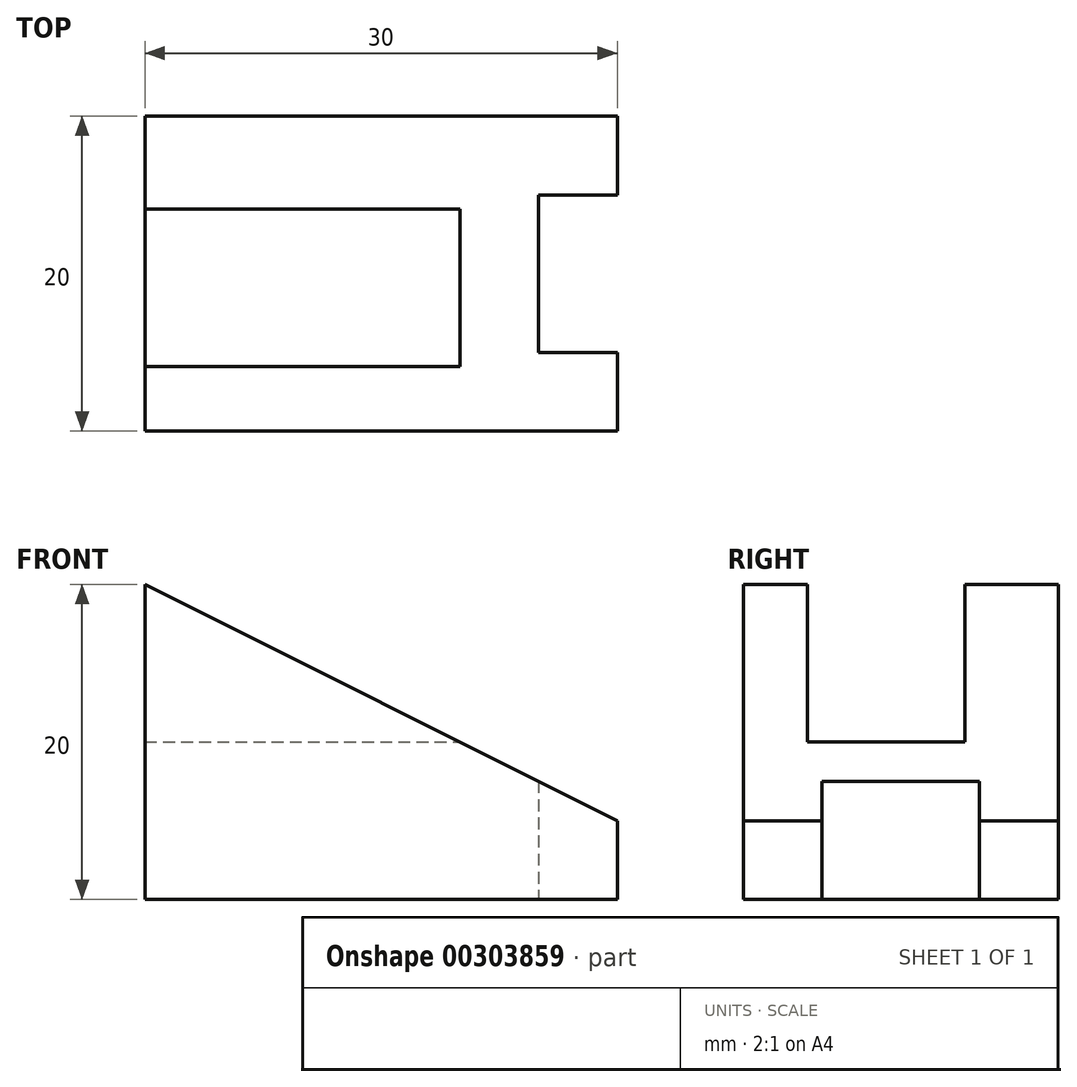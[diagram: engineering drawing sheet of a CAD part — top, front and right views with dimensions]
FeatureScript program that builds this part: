
annotation { "Feature Type Name" : "Feature", "Feature Type Description" : "" }
export const myFeature = defineFeature(function(context is Context, id is Id, definition is map)
    precondition{}
    {
        {
            var Q0;
            Q0=qCreatedBy(makeId("Front.planeOp"),FACE);
            var sketch = newSketch(context, id + "F0", { "sketchPlane" : qUnion([Q0])});
            skLineSegment(sketch, "E0", {"start": v(0, 0) * mm, "end": v(0, 20) * mm});
            skLineSegment(sketch, "E1", {"start": v(0, 0) * mm, "end": v(30, 0) * mm});
            skLineSegment(sketch, "E2", {"start": v(30, 0) * mm, "end": v(30, 5) * mm});
            skLineSegment(sketch, "E3", {"start": v(30, 5) * mm, "end": v(0, 20) * mm});
            skSolve(sketch);
        }
        {
            var Q0;
            Q0=makeQuery(id+"F0.imprint","IMPRINT",FACE,{"disambiguationData":[TD([[makeQuery(id+"F0.imprint","IMPRINT",EDGE,{"derivedFrom":sQuery(id+"F0.wireOp",EDGE,"E0")}),-1.0]])]});
            extrude(context, id + "F1", {"entities" : qUnion([Q0]), "oppositeDirection" : true, "depth" : 20 * mm});
        }
        {
            var Q0;
            Q0=qCreatedBy(makeId("Top.planeOp"),FACE);
            var sketch = newSketch(context, id + "F2", { "sketchPlane" : qUnion([Q0])});
            skLineSegment(sketch, "E4", {"start": v(0, 14.1) * mm, "end": v(20, 14.1) * mm});
            skLineSegment(sketch, "E5", {"start": v(20, 14.1) * mm, "end": v(20, 4.1) * mm});
            skLineSegment(sketch, "E6", {"start": v(20, 4.1) * mm, "end": v(0, 4.1) * mm});
            skLineSegment(sketch, "E7", {"start": v(0, 4.1) * mm, "end": v(0, 14.1) * mm});
            skSolve(sketch);
        }
        {
            var Q0;
            Q0 = qSketchRegion(id + "F2", true);
            extrude(context, id + "F3", {"entities" : qUnion([Q0]), "operationType" : NewBodyOperationType.REMOVE, "depth" : 25 * mm, "hasSecondDirection" : true, "secondDirectionOppositeDirection" : false, "secondDirectionDepth" : 10 * mm});
        }
        {
            var Q0;
            Q0=makeQuery(id+"F1.opExtrude","SWEPT_FACE",FACE,{"disambiguationData":[OSD([sQuery(id+"F0.wireOp",EDGE,"E1")])]});
            var sketch = newSketch(context, id + "F4", { "sketchPlane" : qUnion([Q0])});
            skLineSegment(sketch, "E8", {"start": v(30, 0) * mm, "end": v(30, -5) * mm});
            skLineSegment(sketch, "E9", {"start": v(30, -5) * mm, "end": v(25, -5) * mm});
            skLineSegment(sketch, "E10", {"start": v(25, -5) * mm, "end": v(25, -15) * mm});
            skLineSegment(sketch, "E11", {"start": v(25, -15) * mm, "end": v(33.3, -15) * mm});
            skLineSegment(sketch, "E12", {"start": v(33.3, -15) * mm, "end": v(30, -5) * mm});
            skSolve(sketch);
        }
        {
            var Q0;
            Q0 = qSketchRegion(id + "F4", true);
            extrude(context, id + "F5", {"entities" : qUnion([Q0]), "operationType" : NewBodyOperationType.REMOVE, "oppositeDirection" : true, "depth" : 25 * mm});
        }
    });
